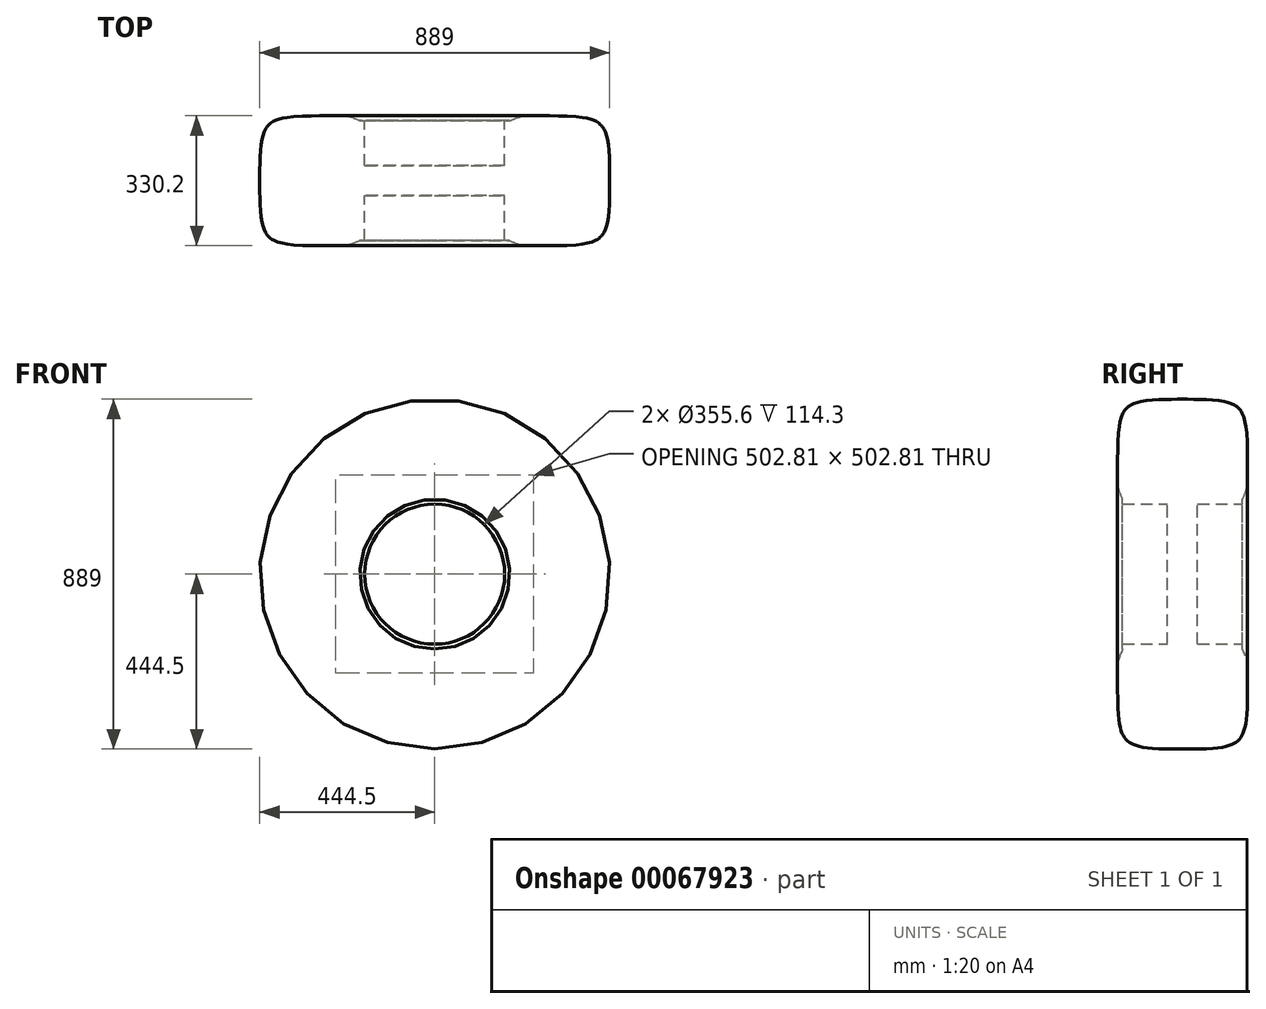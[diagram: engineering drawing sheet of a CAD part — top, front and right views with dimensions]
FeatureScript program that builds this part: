
annotation { "Feature Type Name" : "Feature", "Feature Type Description" : "" }
export const myFeature = defineFeature(function(context is Context, id is Id, definition is map)
    precondition{}
    {
        {
            var Q0;
            Q0=qCreatedBy(makeId("Front.planeOp"),FACE);
            var sketch = newSketch(context, id + "F0", { "sketchPlane" : qUnion([Q0])});
            skCircle(sketch, "E0", {"center": v(0, 0) * mm, "radius": 444.5 * mm});
            skCircle(sketch, "E1", {"center": v(0, 0) * mm, "radius": 190.5 * mm});
            skCircle(sketch, "E2", {"center": v(0, 0) * mm, "radius": 177.8 * mm});
            skSolve(sketch);
        }
        {
            var Q0;
            Q0=makeQuery(id+"F0.imprint","IMPRINT",FACE,{"disambiguationData":[TD([[makeQuery(id+"F0.imprint","IMPRINT",EDGE,{"derivedFrom":sQuery(id+"F0.wireOp",EDGE,"E0")}),1.0]])]});
            extrude(context, id + "F1", {"entities" : qUnion([Q0]), "endBound" : BoundingType.SYMMETRIC, "depth" : 330.2 * mm});
        }
        {
            var Q0;
            Q0=makeQuery(id+"F0.imprint","IMPRINT",FACE,{"disambiguationData":[TD([[makeQuery(id+"F0.imprint","IMPRINT",EDGE,{"derivedFrom":sQuery(id+"F0.wireOp",EDGE,"E1")}),1.0]])]});
            extrude(context, id + "F2", {"entities" : qUnion([Q0]), "operationType" : NewBodyOperationType.ADD, "endBound" : BoundingType.SYMMETRIC, "depth" : 304.8 * mm});
        }
        {
            var Q0;
            Q0=makeQuery(id+"F0.imprint","IMPRINT",FACE,{"disambiguationData":[TD([[makeQuery(id+"F0.imprint","IMPRINT",EDGE,{"derivedFrom":sQuery(id+"F0.wireOp",EDGE,"E2")}),1.0]])]});
            extrude(context, id + "F3", {"entities" : qUnion([Q0]), "operationType" : NewBodyOperationType.ADD, "endBound" : BoundingType.SYMMETRIC, "depth" : 76.2 * mm});
        }
        {
            var Q0;
            Q0=makeQuery(id+"F1.opExtrude","CAP_EDGE",EDGE,{"disambiguationData":[OSD([sQuery(id+"F0.wireOp",EDGE,"E0")])],"isStart":false});
            var Q1;
            Q1=makeQuery(id+"F1.opExtrude","CAP_EDGE",EDGE,{"disambiguationData":[OSD([sQuery(id+"F0.wireOp",EDGE,"E0")])],"isStart":true});
            var Q2;
            Q2=makeQuery(id+"F1.opExtrude","CAP_EDGE",EDGE,{"disambiguationData":[OSD([sQuery(id+"F0.wireOp",EDGE,"E1")])],"isStart":false});
            var Q3;
            Q3=makeQuery(id+"F1.opExtrude","CAP_EDGE",EDGE,{"disambiguationData":[OSD([sQuery(id+"F0.wireOp",EDGE,"E1")])],"isStart":true});
            fillet(context, id + "F4", {"entities" : qUnion([Q0, Q1, Q2, Q3]), "radius" : 152.4 * mm, "tangentPropagation" : true, "rho" : 0.7, "crossSection" : FilletCrossSection.CONIC, "allowEdgeOverflow" : false});
        }
    });
